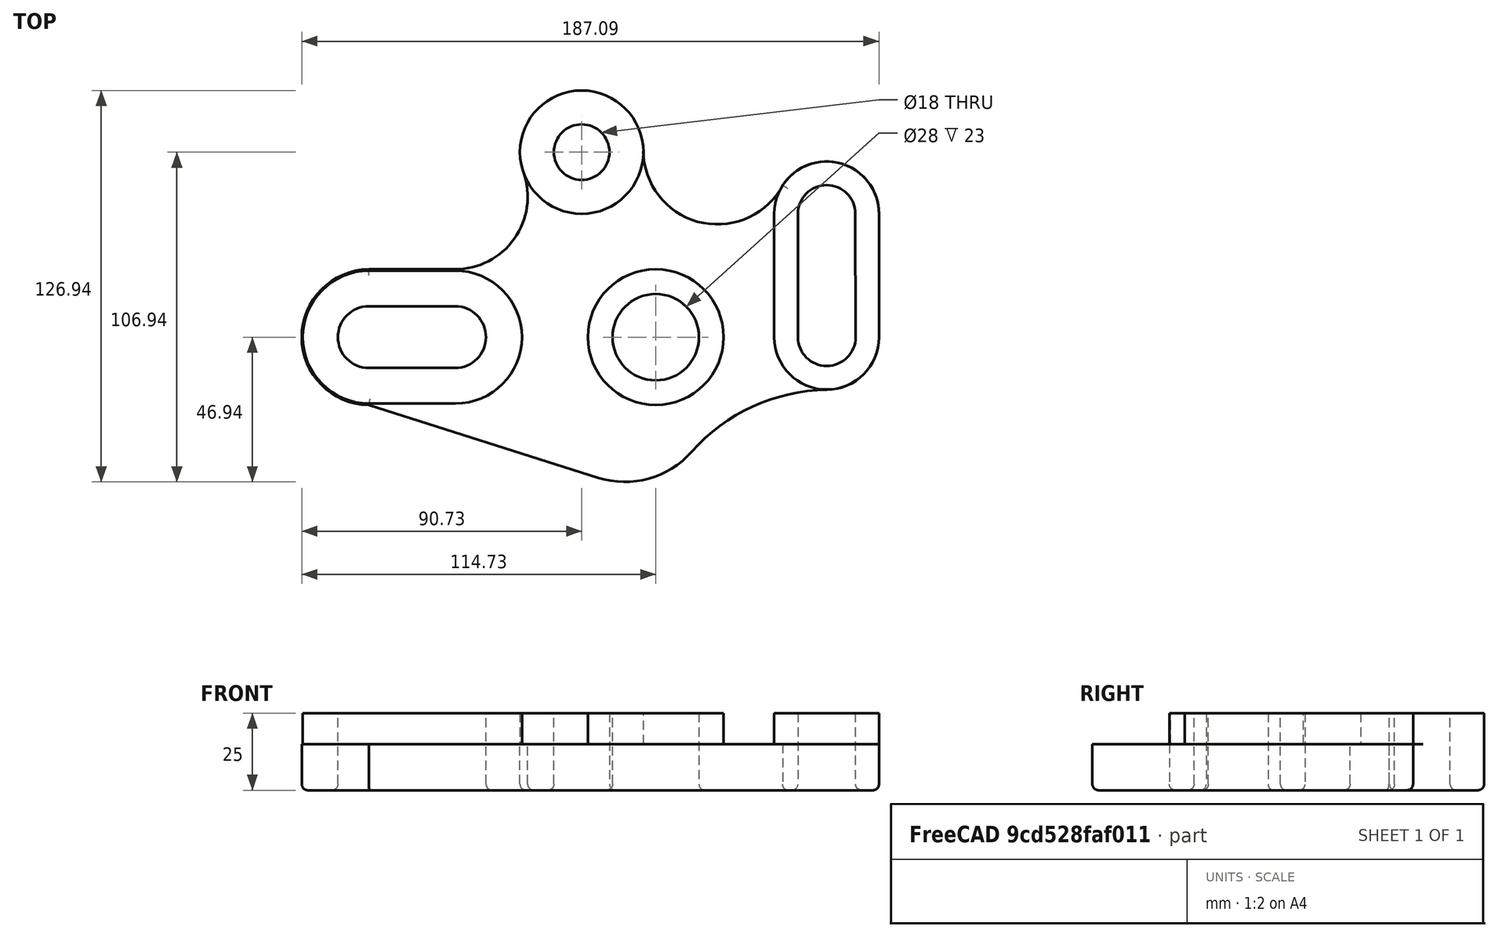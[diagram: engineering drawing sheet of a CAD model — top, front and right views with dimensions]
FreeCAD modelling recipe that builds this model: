
FCSTD DOCUMENT  (FreeCAD 0.19R24267 +148 (Git))
Label: Idler Plate
License: All rights reserved
LicenseURL: http://en.wikipedia.org/wiki/All_rights_reserved
objects: TechDraw::DrawViewDimension×26, Sketcher::SketchObject×4, PartDesign::Pad×2, PartDesign::Plane×1, Part::Part2DObjectPython×1, PartDesign::Pocket×1, PartDesign::Fillet×1, PartDesign::Body×1, TechDraw::DrawSVGTemplate×1, TechDraw::DrawViewPart×1, TechDraw::DrawPage×1
note: 15 computed .brp shape members not serialized (recipe doc carries the construction recipe); baked Part::Feature solids carry a one-line shape summary decoded from their .brp

FEATURE [Sketcher::SketchObject] Sketch
  FullyConstrained = false
  MapMode = 5
  Support = -> [XY_Plane]
  sketch-geometry (25):
    g0: Circle CenterX=-24 CenterY=60 CenterZ=0 NormalX=0 NormalY=0 NormalZ=1 AngleXU=0 Radius=20
    g1: Circle CenterX=0 CenterY=0 CenterZ=0 NormalX=0 NormalY=0 NormalZ=1 AngleXU=0 Radius=22
    g2: Circle CenterX=0 CenterY=0 CenterZ=0 NormalX=0 NormalY=0 NormalZ=1 AngleXU=0 Radius=14
    g3: Circle CenterX=-24 CenterY=60 CenterZ=0 NormalX=0 NormalY=0 NormalZ=1 AngleXU=0 Radius=9
    g4: ArcOfCircle CenterX=-93 CenterY=0 CenterZ=0 NormalX=0 NormalY=0 NormalZ=1 AngleXU=0 Radius=22 StartAngle=1.5708 EndAngle=4.71239
    g5: ArcOfCircle CenterX=-65 CenterY=-1.6e-15 CenterZ=0 NormalX=0 NormalY=0 NormalZ=1 AngleXU=0 Radius=22 StartAngle=4.71239 EndAngle=7.85398
    g6: LineSegment StartX=-93 StartY=-22 StartZ=0 EndX=-65 EndY=-22 EndZ=0
    g7: LineSegment StartX=-93 StartY=22 StartZ=0 EndX=-65 EndY=22 EndZ=0
    g8: ArcOfCircle CenterX=-93 CenterY=0 CenterZ=0 NormalX=0 NormalY=0 NormalZ=1 AngleXU=0 Radius=10 StartAngle=1.5708 EndAngle=4.71239
    g9: ArcOfCircle CenterX=-65 CenterY=-1.6e-15 CenterZ=0 NormalX=0 NormalY=0 NormalZ=1 AngleXU=0 Radius=10 StartAngle=4.71239 EndAngle=7.85398
    g10: LineSegment StartX=-93 StartY=-10 StartZ=0 EndX=-65 EndY=-10 EndZ=0
    g11: LineSegment StartX=-93 StartY=10 StartZ=0 EndX=-65 EndY=10 EndZ=0
    g12: ArcOfCircle CenterX=55.3868 CenterY=0 CenterZ=0 NormalX=0 NormalY=0 NormalZ=1 AngleXU=0 Radius=16.975 StartAngle=3.14159 EndAngle=6.28319
    g13: ArcOfCircle CenterX=55.3868 CenterY=40 CenterZ=0 NormalX=0 NormalY=0 NormalZ=1 AngleXU=0 Radius=16.975 StartAngle=0 EndAngle=3.14159
    g14: LineSegment StartX=72.3617 StartY=-4.2e-15 StartZ=0 EndX=72.3617 EndY=40 EndZ=0
    g15: LineSegment StartX=38.4118 StartY=2.1e-15 StartZ=0 EndX=38.4118 EndY=40 EndZ=0
    g16: ArcOfCircle CenterX=55.3868 CenterY=0 CenterZ=0 NormalX=0 NormalY=0 NormalZ=1 AngleXU=0 Radius=9.30464 StartAngle=3.14159 EndAngle=6.28319
    g17: ArcOfCircle CenterX=55.3868 CenterY=40 CenterZ=0 NormalX=0 NormalY=0 NormalZ=1 AngleXU=0 Radius=9.30464 StartAngle=2e-16 EndAngle=3.14159
    g18: LineSegment StartX=64.6914 StartY=-2.3e-15 StartZ=0 EndX=64.6914 EndY=40 EndZ=0
    g19: LineSegment StartX=46.0821 StartY=5.3e-15 StartZ=0 EndX=46.0821 EndY=40 EndZ=0
    g20: ArcOfCircle CenterX=-65 CenterY=45.4914 CenterZ=0 NormalX=0 NormalY=0 NormalZ=1 AngleXU=0 Radius=23.4914 StartAngle=4.71239 EndAngle=6.6233
    g21: ArcOfCircle CenterX=19.9961 CenterY=60.5875 CenterZ=0 NormalX=0 NormalY=0 NormalZ=1 AngleXU=0 Radius=24 StartAngle=3.15495 EndAngle=5.78943
    g22: LineSegment StartX=-93 StartY=-22 StartZ=0 EndX=-18.6679 EndY=-45.5803 EndZ=0
    g23: ArcOfCircle CenterX=56.0281 CenterY=-76.4776 CenterZ=0 NormalX=0 NormalY=0 NormalZ=1 AngleXU=0 Radius=59.5054 StartAngle=1.57918 EndAngle=2.41234
    g24: ArcOfCircle CenterX=-10.0673 CenterY=-18.4687 CenterZ=0 NormalX=0 NormalY=0 NormalZ=1 AngleXU=0 Radius=28.4431 StartAngle=4.4052 EndAngle=5.58151
  constraints (55):
    c: Coincident(g1,g-1)
    c: Coincident(g2,g1)
    c: Diameter(g1) = 44
    c: Diameter(g2) = 28
    c: Diameter(g0) = 40
    c: Coincident(g3,g0)
    c: Diameter(g3) = 18
    c: DistanceX(g0,g1) = 24
    c: DistanceY(g1,g0) = 60
    c: Tangent(g4,g7) = 1.5708
    c: Tangent(g4,g6) = -1.5708
    c: Tangent(g6,g5) = -1.5708
    c: Tangent(g7,g5) = 1.5708
    c: Horizontal(g6)
    c: Equal(g4,g5)
    c: PointOnObject(g4,g-1)
    c: Tangent(g8,g11) = 1.5708
    c: Tangent(g8,g10) = -1.5708
    c: Tangent(g10,g9) = -1.5708
    c: Tangent(g11,g9) = 1.5708
    c: Horizontal(g10)
    c: Coincident(g8,g4)
    c: Coincident(g5,g9)
    c: Radius(g4) = 22
    c: Radius(g8) = 10
    c: DistanceX(g4,g5) = 28
    c: Tangent(g12,g15) = 1.5708
    c: Tangent(g12,g14) = -1.5708
    c: Tangent(g14,g13) = -1.5708
    c: Tangent(g15,g13) = 1.5708
    c: Vertical(g14)
    c: Equal(g12,g13)
    c: PointOnObject(g12,g-1)
    c: Tangent(g16,g19) = 1.5708
    c: Tangent(g16,g18) = -1.5708
    c: Tangent(g18,g17) = -1.5708
    c: Tangent(g19,g17) = 1.5708
    c: Vertical(g18)
    c: Coincident(g16,g12)
    c: Coincident(g13,g17)
    c: DistanceY(g12,g13) = 40
    c: Coincident(g20,g5)
    c: PointOnObject(g20,g0)
    c: PointOnObject(g21,g13)
    c: PointOnObject(g21,g0)
    c: Tangent(g0,g21)
    c: Radius(g21) = 24
    c: Coincident(g22,g4)
    c: PointOnObject(g23,g12)
    c: Tangent(g23,g12)
    c: Coincident(g24,g23)
    c: Tangent(g24,g22) = -1.5708
    c: DistanceX(g5,g1) = 65
    c: Tangent(g0,g20)
    c: Tangent(g20,g7)
FEATURE [Sketcher::SketchObject] Sketch001
  ExternalGeometry = -> [Sketch]
  FullyConstrained = false
  MapMode = 5
  Support = -> [XY_Plane]
  sketch-geometry (11):
    g0: ArcOfCircle CenterX=-24 CenterY=60 CenterZ=0 NormalX=0 NormalY=0 NormalZ=1 AngleXU=0 Radius=20 StartAngle=0.0133524 EndAngle=3.48171
    g1: ArcOfCircle CenterX=19.9961 CenterY=60.5875 CenterZ=0 NormalX=0 NormalY=0 NormalZ=1 AngleXU=0 Radius=24 StartAngle=3.15495 EndAngle=5.78943
    g2: ArcOfCircle CenterX=55.3868 CenterY=40 CenterZ=0 NormalX=0 NormalY=0 NormalZ=1 AngleXU=0 Radius=16.975 StartAngle=-9e-16 EndAngle=2.5679
    g3: ArcOfCircle CenterX=55.248 CenterY=9.24041e-07 CenterZ=0 NormalX=0 NormalY=0 NormalZ=1 AngleXU=0 Radius=17.1138 StartAngle=4.7237 EndAngle=6.28319
    g4: ArcOfCircle CenterX=56.1121 CenterY=-76.3799 CenterZ=0 NormalX=0 NormalY=0 NormalZ=1 AngleXU=0 Radius=59.2711 StartAngle=1.58211 EndAngle=2.41888
    g5: ArcOfCircle CenterX=-9.97263 CenterY=-18.1014 CenterZ=0 NormalX=0 NormalY=0 NormalZ=1 AngleXU=0 Radius=28.8401 StartAngle=4.40589 EndAngle=5.56047
    g6: LineSegment StartX=-93 StartY=-22 StartZ=0 EndX=-18.6743 EndY=-45.5974 EndZ=0
    g7: ArcOfCircle CenterX=-92.7237 CenterY=2.42114e-05 CenterZ=0 NormalX=0 NormalY=0 NormalZ=1 AngleXU=0 Radius=22.0018 StartAngle=1.58353 EndAngle=4.69983
    g8: LineSegment StartX=72.3617 StartY=40 StartZ=0 EndX=72.3617 EndY=-5.68e-14 EndZ=0
    g9: LineSegment StartX=-93.0038 StartY=22 StartZ=0 EndX=-65 EndY=22 EndZ=0
    g10: ArcOfCircle CenterX=-65 CenterY=45.4914 CenterZ=0 NormalX=0 NormalY=0 NormalZ=1 AngleXU=0 Radius=23.4914 StartAngle=4.71239 EndAngle=6.6233
  constraints (24):
    c: Coincident(g0,g-13)
    c: Coincident(g0,g-4)
    c: Tangent(g0,g-3)
    c: Coincident(g1,g0)
    c: Coincident(g1,g-4)
    c: Tangent(g1,g-4)
    c: Coincident(g2,g1)
    c: Coincident(g2,g-6)
    c: Tangent(g2,g-5)
    c: Coincident(g3,g-7)
    c: Tangent(g3,g-7)
    c: Coincident(g7,g6)
    c: Coincident(g5,g6)
    c: Coincident(g8,g2)
    c: Coincident(g8,g3)
    c: Tangent(g4,g5) = 1.5708
    c: Tangent(g4,g3) = 1.5708
    c: Coincident(g6,g-11)
    c: Coincident(g9,g7)
    c: Coincident(g9,g-13)
    c: Horizontal(g9)
    c: Coincident(g10,g9)
    c: Coincident(g10,g0)
    c: Tangent(g10,g-13)
FEATURE [PartDesign::Pad] Pad
  Direction = (1,1,1)
  Length = 15
  Length2 = 100
  Profile = -> Sketch001
  Reversed = true
  Type = 0
FEATURE [Sketcher::SketchObject] Sketch002
  ExternalGeometry = -> [Sketch]
  FullyConstrained = false
  MapMode = 5
  Support = -> [XY_Plane]
  sketch-geometry (10):
    g0: Circle CenterX=0 CenterY=0 CenterZ=0 NormalX=0 NormalY=0 NormalZ=1 AngleXU=0 Radius=22
    g1: ArcOfCircle CenterX=55.3834 CenterY=-0.000158297 CenterZ=0 NormalX=0 NormalY=0 NormalZ=1 AngleXU=0 Radius=16.9716 StartAngle=3.14159 EndAngle=6.28319
    g2: ArcOfCircle CenterX=55.3834 CenterY=39.9998 CenterZ=0 NormalX=0 NormalY=0 NormalZ=1 AngleXU=0 Radius=16.9716 StartAngle=2.61945e-11 EndAngle=3.14159
    g3: LineSegment StartX=72.3549 StartY=-0.000158298 StartZ=0 EndX=72.3549 EndY=39.9998 EndZ=0
    g4: LineSegment StartX=38.4118 StartY=-0.000158298 StartZ=0 EndX=38.4118 EndY=39.9998 EndZ=0
    g5: ArcOfCircle CenterX=-64.8801 CenterY=0 CenterZ=0 NormalX=0 NormalY=0 NormalZ=1 AngleXU=0 Radius=21.5308 StartAngle=4.71239 EndAngle=7.85398
    g6: ArcOfCircle CenterX=-92.8801 CenterY=-1.3e-15 CenterZ=0 NormalX=0 NormalY=0 NormalZ=1 AngleXU=0 Radius=21.5308 StartAngle=1.5708 EndAngle=4.71239
    g7: LineSegment StartX=-64.8801 StartY=21.5308 StartZ=0 EndX=-92.8801 EndY=21.5308 EndZ=0
    g8: LineSegment StartX=-64.8801 StartY=-21.5308 StartZ=0 EndX=-92.8801 EndY=-21.5308 EndZ=0
    g9: Circle CenterX=-24 CenterY=60 CenterZ=0 NormalX=0 NormalY=0 NormalZ=1 AngleXU=0 Radius=20
  constraints (20):
    c: Coincident(g0,g-1)
    c: Tangent(g1,g4) = 1.5708
    c: Tangent(g1,g3) = -1.5708
    c: Tangent(g3,g2) = -1.5708
    c: Tangent(g4,g2) = 1.5708
    c: Vertical(g3)
    c: Equal(g1,g2)
    c: PointOnObject(g2,g-7)
    c: Tangent(g5,g8) = 1.5708
    c: Tangent(g5,g7) = -1.5708
    c: Tangent(g7,g6) = -1.5708
    c: Tangent(g8,g6) = 1.5708
    c: Horizontal(g7)
    c: Equal(g5,g6)
    c: PointOnObject(g5,g-1)
    c: DistanceX(g6,g5) = 28
    c: DistanceY(g1,g2) = 40
    c: Coincident(g9,g-8)
    c: Diameter(g9) = 40
    c: Diameter(g0) = 44
FEATURE [PartDesign::Pad] Pad001
  BaseFeature = -> Pad
  Direction = (1,1,1)
  Length = 10
  Length2 = 100
  Profile = -> Sketch002
  Type = 0
FEATURE [PartDesign::Plane] DatumPlane
  Length = 217.722
  MapMode = 5
  Placement = pos=(0,0,10) rot=(0,0,1;0rad)
  ResizeMode = 0
  Support = -> [Pad001]
  Width = 157.601
FEATURE [Sketcher::SketchObject] Sketch003
  ExternalGeometry = -> [Sketch]
  FullyConstrained = false
  MapMode = 5
  Placement = pos=(0,0,10) rot=(0,0,1;0rad)
  Support = -> [DatumPlane]
  sketch-geometry (10):
    g0: Circle CenterX=0 CenterY=0 CenterZ=0 NormalX=0 NormalY=0 NormalZ=1 AngleXU=0 Radius=14
    g1: Circle CenterX=-24 CenterY=60 CenterZ=0 NormalX=0 NormalY=0 NormalZ=1 AngleXU=0 Radius=9
    g2: ArcOfCircle CenterX=-65 CenterY=0 CenterZ=0 NormalX=0 NormalY=0 NormalZ=1 AngleXU=0 Radius=10 StartAngle=4.71239 EndAngle=7.85398
    g3: ArcOfCircle CenterX=-93 CenterY=4.585e-13 CenterZ=0 NormalX=0 NormalY=0 NormalZ=1 AngleXU=0 Radius=10 StartAngle=1.5708 EndAngle=4.71239
    g4: LineSegment StartX=-65 StartY=10 StartZ=0 EndX=-93 EndY=10 EndZ=0
    g5: LineSegment StartX=-65 StartY=-10 StartZ=0 EndX=-93 EndY=-10 EndZ=0
    g6: ArcOfCircle CenterX=55.4299 CenterY=1.4e-15 CenterZ=0 NormalX=0 NormalY=0 NormalZ=1 AngleXU=0 Radius=9.34777 StartAngle=3.14159 EndAngle=6.27883
    g7: ArcOfCircle CenterX=55.3868 CenterY=40 CenterZ=0 NormalX=0 NormalY=0 NormalZ=1 AngleXU=0 Radius=9.30464 StartAngle=0 EndAngle=3.14159
    g8: LineSegment StartX=64.7776 StartY=-0.04075 StartZ=0 EndX=64.6914 EndY=40 EndZ=0
    g9: LineSegment StartX=46.0821 StartY=5.3e-15 StartZ=0 EndX=46.0821 EndY=40 EndZ=0
  constraints (21):
    c: Coincident(g0,g-1)
    c: Diameter(g0) = 28
    c: Coincident(g1,g-3)
    c: Diameter(g1) = 18
    c: Tangent(g2,g5) = 1.5708
    c: Tangent(g2,g4) = -1.5708
    c: Tangent(g4,g3) = -1.5708
    c: Tangent(g5,g3) = 1.5708
    c: Horizontal(g4)
    c: Equal(g2,g3)
    c: PointOnObject(g2,g-1)
    c: Distance(g2,g3) = 28
    c: Diameter(g3) = 20
    c: DistanceX(g2,g0) = 65
    c: Tangent(g6,g9) = 1.5708
    c: Tangent(g9,g7) = 1.5708
    c: Coincident(g7,g-5)
    c: Coincident(g6,g-7)
    c: Coincident(g7,g8)
    c: Coincident(g7,g-6)
    c: Coincident(g8,g6)
FEATURE [Part::Part2DObjectPython] Clone2D  label="Sketch (2D)"  # Draft 2D object (typed FeaturePython)
  Fuse = false
  Objects = -> [Sketch]
  Scale = (1,1,1)
FEATURE [PartDesign::Pocket] Pocket
  BaseFeature = -> Pad001
  Length = 3
  Length2 = 100
  Profile = -> Sketch003
  Type = 1
FEATURE [PartDesign::Fillet] Fillet
  Base = -> Pocket [Edge33,Edge35,Edge37,Edge41,Edge42,Edge39,Edge40,Edge38,Edge36,Edge48,Edge43,Edge34,Edge32,Edge10,Edge4,Edge7,Edge31,Edge47,Edge46,Edge45,Edge44]
  BaseFeature = -> Pocket
  Radius = 2
  SupportTransform = false
FEATURE [PartDesign::Body] Body
  Group = -> [Sketch,Sketch001,Pad,Sketch002,Pad001,DatumPlane,Sketch003,Clone2D,Pocket,Fillet]
  Origin = -> Origin
  Tip = -> Fillet
FEATURE [TechDraw::DrawSVGTemplate] Template
  EditableTexts = Designed_by_Name=Designed by Name; Drawing_number=Drawing number; FC-Date=Date; FC-SC=Scale; FC-SH=Sheet; FC-Title=Title; Subtitle=Subtitle; Weight=Weight
  Height = 210
  Orientation = 1
  Width = 297
FEATURE [TechDraw::DrawViewPart] View  label="Top view"
  CoarseView = false
  Direction = (0,0,1)
  Focus = 100
  HardHidden = false
  IsoCount = 0
  IsoHidden = false
  IsoVisible = false
  LockPosition = false
  Perspective = false
  Rotation = 0
  ScaleType = 0
  SeamHidden = false
  SeamVisible = true
  SmoothHidden = false
  SmoothVisible = true
  Source = -> [Fillet]
  X = 110.865
  XDirection = (-1,0,0)
  Y = 128.572
FEATURE [TechDraw::DrawViewDimension] Dimension
  Arbitrary = false
  ArbitraryTolerances = false
  EqualTolerance = true
  FormatSpec = ⌀%.2f
  FormatSpecOverTolerance = %+.2f
  FormatSpecUnderTolerance = %+.2f
  Inverted = false
  LockPosition = false
  MeasureType = 1
  OverTolerance = 0
  References2D = -> [View]
  Rotation = 0
  ScaleType = 0
  TheoreticalExact = false
  Type = 5
  UnderTolerance = 0
  X = -39.4982
  Y = 38.3834
FEATURE [TechDraw::DrawViewDimension] Dimension001
  Arbitrary = false
  ArbitraryTolerances = false
  EqualTolerance = true
  FormatSpec = ⌀%.2f
  FormatSpecOverTolerance = %+.2f
  FormatSpecUnderTolerance = %+.2f
  Inverted = false
  LockPosition = false
  MeasureType = 1
  OverTolerance = 0
  References2D = -> [View]
  Rotation = 0
  ScaleType = 0
  TheoreticalExact = false
  Type = 5
  UnderTolerance = 0
  X = 7.12678
  Y = 44.872
FEATURE [TechDraw::DrawViewDimension] Dimension002
  Arbitrary = false
  ArbitraryTolerances = false
  EqualTolerance = true
  FormatSpec = %.2f
  FormatSpecOverTolerance = %+.2f
  FormatSpecUnderTolerance = %+.2f
  Inverted = false
  LockPosition = false
  MeasureType = 1
  OverTolerance = 0
  References2D = -> [View]
  Rotation = 0
  ScaleType = 0
  TheoreticalExact = false
  Type = 6
  UnderTolerance = 0
  X = 18.4646
  Y = 51.2195
FEATURE [TechDraw::DrawViewDimension] Dimension003
  Arbitrary = false
  ArbitraryTolerances = false
  EqualTolerance = true
  FormatSpec = R%.2f
  FormatSpecOverTolerance = %+.2f
  FormatSpecUnderTolerance = %+.2f
  Inverted = false
  LockPosition = false
  MeasureType = 1
  OverTolerance = 0
  References2D = -> [View]
  Rotation = 0
  ScaleType = 0
  TheoreticalExact = false
  Type = 4
  UnderTolerance = 0
  X = -80.4146
  Y = 59.9268
FEATURE [TechDraw::DrawViewDimension] Dimension004
  Arbitrary = false
  ArbitraryTolerances = false
  EqualTolerance = true
  FormatSpec = R%.2f
  FormatSpecOverTolerance = %+.2f
  FormatSpecUnderTolerance = %+.2f
  Inverted = false
  LockPosition = false
  MeasureType = 1
  OverTolerance = 0
  References2D = -> [View]
  Rotation = 0
  ScaleType = 0
  TheoreticalExact = false
  Type = 4
  UnderTolerance = 0
  X = -26.3197
  Y = 57.6329
FEATURE [TechDraw::DrawViewDimension] Dimension005
  Arbitrary = false
  ArbitraryTolerances = false
  EqualTolerance = true
  FormatSpec = ⌀%.2f
  FormatSpecOverTolerance = %+.2f
  FormatSpecUnderTolerance = %+.2f
  Inverted = false
  LockPosition = false
  MeasureType = 1
  OverTolerance = 0
  References2D = -> [View]
  Rotation = 0
  ScaleType = 0
  TheoreticalExact = false
  Type = 5
  UnderTolerance = 0
  X = 3.22632
  Y = -6.83704
FEATURE [TechDraw::DrawViewDimension] Dimension006
  Arbitrary = false
  ArbitraryTolerances = false
  EqualTolerance = true
  FormatSpec = ⌀%.2f
  FormatSpecOverTolerance = %+.2f
  FormatSpecUnderTolerance = %+.2f
  Inverted = false
  LockPosition = false
  MeasureType = 1
  OverTolerance = 0
  References2D = -> [View]
  Rotation = 0
  ScaleType = 0
  TheoreticalExact = false
  Type = 5
  UnderTolerance = 0
  X = 12.8049
  Y = -4.60976
FEATURE [TechDraw::DrawViewDimension] Dimension007
  Arbitrary = false
  ArbitraryTolerances = false
  EqualTolerance = true
  FormatSpec = R%.2f
  FormatSpecOverTolerance = %+.2f
  FormatSpecUnderTolerance = %+.2f
  Inverted = false
  LockPosition = false
  MeasureType = 1
  OverTolerance = 0
  References2D = -> [View]
  Rotation = 0
  ScaleType = 0
  TheoreticalExact = false
  Type = 4
  UnderTolerance = 0
  X = -54.8941
  Y = 33.9773
FEATURE [TechDraw::DrawViewDimension] Dimension008
  Arbitrary = false
  ArbitraryTolerances = false
  EqualTolerance = true
  FormatSpec = R%.2f
  FormatSpecOverTolerance = %+.2f
  FormatSpecUnderTolerance = %+.2f
  Inverted = false
  LockPosition = false
  MeasureType = 1
  OverTolerance = 0
  References2D = -> [View]
  Rotation = 0
  ScaleType = 0
  TheoreticalExact = false
  Type = 4
  UnderTolerance = 0
  X = -83.1947
  Y = 40.3427
FEATURE [TechDraw::DrawViewDimension] Dimension009
  Arbitrary = false
  ArbitraryTolerances = false
  EqualTolerance = true
  FormatSpec = R%.2f
  FormatSpecOverTolerance = %+.2f
  FormatSpecUnderTolerance = %+.2f
  Inverted = false
  LockPosition = false
  MeasureType = 1
  OverTolerance = 0
  References2D = -> [View]
  Rotation = 0
  ScaleType = 0
  TheoreticalExact = false
  Type = 4
  UnderTolerance = 0
  X = 52.7561
  Y = -32.7805
FEATURE [TechDraw::DrawViewDimension] Dimension010
  Arbitrary = false
  ArbitraryTolerances = false
  EqualTolerance = true
  FormatSpec = R%.2f
  FormatSpecOverTolerance = %+.2f
  FormatSpecUnderTolerance = %+.2f
  Inverted = false
  LockPosition = false
  MeasureType = 1
  OverTolerance = 0
  References2D = -> [View]
  Rotation = 0
  ScaleType = 0
  TheoreticalExact = false
  Type = 4
  UnderTolerance = 0
  X = -42.8604
  Y = -5.8446
FEATURE [TechDraw::DrawViewDimension] Dimension012
  Arbitrary = false
  ArbitraryTolerances = false
  EqualTolerance = true
  FormatSpec = %.2f
  FormatSpecOverTolerance = %+.2f
  FormatSpecUnderTolerance = %+.2f
  Inverted = false
  LockPosition = false
  MeasureType = 1
  OverTolerance = 0
  References2D = -> [View]
  Rotation = 0
  ScaleType = 0
  TheoreticalExact = false
  Type = 1
  UnderTolerance = 0
  X = -90.2951
  Y = -50.3832
FEATURE [TechDraw::DrawViewDimension] Dimension013
  Arbitrary = false
  ArbitraryTolerances = false
  EqualTolerance = true
  FormatSpec = %.2f
  FormatSpecOverTolerance = %+.2f
  FormatSpecUnderTolerance = %+.2f
  Inverted = false
  LockPosition = false
  MeasureType = 1
  OverTolerance = 0
  References2D = -> [View]
  Rotation = 0
  ScaleType = 0
  TheoreticalExact = false
  Type = 2
  UnderTolerance = 0
  X = 63.765
  Y = -14.4595
FEATURE [TechDraw::DrawViewDimension] Dimension014
  Arbitrary = false
  ArbitraryTolerances = false
  EqualTolerance = true
  FormatSpec = %.2f
  FormatSpecOverTolerance = %+.2f
  FormatSpecUnderTolerance = %+.2f
  Inverted = false
  LockPosition = false
  MeasureType = 1
  OverTolerance = 0
  References2D = -> [View]
  Rotation = 0
  ScaleType = 0
  TheoreticalExact = false
  Type = 1
  UnderTolerance = 0
  X = 36.7328
  Y = 64.093
FEATURE [TechDraw::DrawViewDimension] Dimension015
  Arbitrary = false
  ArbitraryTolerances = false
  EqualTolerance = true
  FormatSpec = R%.2f
  FormatSpecOverTolerance = %+.2f
  FormatSpecUnderTolerance = %+.2f
  Inverted = false
  LockPosition = false
  MeasureType = 1
  OverTolerance = 0
  References2D = -> [View]
  Rotation = 0
  ScaleType = 0
  TheoreticalExact = false
  Type = 4
  UnderTolerance = 0
  X = 50.0298
  Y = 23.3784
FEATURE [TechDraw::DrawViewDimension] Dimension016
  Arbitrary = false
  ArbitraryTolerances = false
  EqualTolerance = true
  FormatSpec = R%.2f
  FormatSpecOverTolerance = %+.2f
  FormatSpecUnderTolerance = %+.2f
  Inverted = false
  LockPosition = false
  MeasureType = 1
  OverTolerance = 0
  References2D = -> [View]
  Rotation = 0
  ScaleType = 0
  TheoreticalExact = false
  Type = 4
  UnderTolerance = 0
  X = 46.2892
  Y = 32.7298
FEATURE [TechDraw::DrawViewDimension] Dimension017
  Arbitrary = false
  ArbitraryTolerances = false
  EqualTolerance = true
  FormatSpec = %.2f
  FormatSpecOverTolerance = %+.2f
  FormatSpecUnderTolerance = %+.2f
  Inverted = false
  LockPosition = false
  MeasureType = 1
  OverTolerance = 0
  References2D = -> [View]
  Rotation = 0
  ScaleType = 0
  TheoreticalExact = false
  Type = 1
  UnderTolerance = 0
  X = 57.4978
  Y = -5.57445
FEATURE [TechDraw::DrawViewDimension] Dimension018
  Arbitrary = false
  ArbitraryTolerances = false
  EqualTolerance = true
  FormatSpec = %.2f
  FormatSpecOverTolerance = %+.2f
  FormatSpecUnderTolerance = %+.2f
  Inverted = false
  LockPosition = false
  MeasureType = 1
  OverTolerance = 0
  References2D = -> [View]
  Rotation = 0
  ScaleType = 0
  TheoreticalExact = false
  Type = 1
  UnderTolerance = 0
  X = -62.6941
  Y = -60.5139
FEATURE [TechDraw::DrawViewDimension] Dimension019
  Arbitrary = false
  ArbitraryTolerances = false
  EqualTolerance = true
  FormatSpec = %.2f
  FormatSpecOverTolerance = %+.2f
  FormatSpecUnderTolerance = %+.2f
  Inverted = false
  LockPosition = false
  MeasureType = 1
  OverTolerance = 0
  References2D = -> [View]
  Rotation = 0
  ScaleType = 0
  TheoreticalExact = false
  Type = 2
  UnderTolerance = 0
  X = 97.274
  Y = -3.08202
FEATURE [TechDraw::DrawViewDimension] Dimension020
  Arbitrary = false
  ArbitraryTolerances = false
  EqualTolerance = true
  FormatSpec = %.2f
  FormatSpecOverTolerance = %+.2f
  FormatSpecUnderTolerance = %+.2f
  Inverted = false
  LockPosition = false
  MeasureType = 1
  OverTolerance = 0
  References2D = -> [View]
  Rotation = 0
  ScaleType = 0
  TheoreticalExact = false
  Type = 2
  UnderTolerance = 0
  X = 98.2091
  Y = 32.1894
FEATURE [TechDraw::DrawViewDimension] Dimension021
  Arbitrary = false
  ArbitraryTolerances = false
  EqualTolerance = true
  FormatSpec = %.2f
  FormatSpecOverTolerance = %+.2f
  FormatSpecUnderTolerance = %+.2f
  Inverted = false
  LockPosition = false
  MeasureType = 1
  OverTolerance = 0
  References2D = -> [View]
  Rotation = 0
  ScaleType = 0
  TheoreticalExact = false
  Type = 0
  UnderTolerance = 0
  X = 67.085
  Y = -55.138
FEATURE [TechDraw::DrawViewDimension] Dimension022
  Arbitrary = false
  ArbitraryTolerances = false
  EqualTolerance = true
  FormatSpec = %.2f
  FormatSpecOverTolerance = %+.2f
  FormatSpecUnderTolerance = %+.2f
  Inverted = false
  LockPosition = false
  MeasureType = 1
  OverTolerance = 0
  References2D = -> [View]
  Rotation = 0
  ScaleType = 0
  TheoreticalExact = false
  Type = 0
  UnderTolerance = 0
  X = -43.22
  Y = -43.7934
FEATURE [TechDraw::DrawViewDimension] Dimension023
  Arbitrary = false
  ArbitraryTolerances = false
  EqualTolerance = true
  FormatSpec = %.2f
  FormatSpecOverTolerance = %+.2f
  FormatSpecUnderTolerance = %+.2f
  Inverted = false
  LockPosition = false
  MeasureType = 1
  OverTolerance = 0
  References2D = -> [View]
  Rotation = 0
  ScaleType = 0
  TheoreticalExact = false
  Type = 0
  UnderTolerance = 0
  X = -61.4779
  Y = 56.193
FEATURE [TechDraw::DrawViewDimension] Dimension024
  Arbitrary = false
  ArbitraryTolerances = false
  EqualTolerance = true
  FormatSpec = %.2f
  FormatSpecOverTolerance = %+.2f
  FormatSpecUnderTolerance = %+.2f
  Inverted = false
  LockPosition = false
  MeasureType = 1
  OverTolerance = 0
  References2D = -> [View]
  Rotation = 0
  ScaleType = 0
  TheoreticalExact = false
  Type = 0
  UnderTolerance = 0
  X = -10.8605
  Y = 50.33
FEATURE [TechDraw::DrawViewDimension] Dimension025
  Arbitrary = false
  ArbitraryTolerances = false
  EqualTolerance = true
  FormatSpec = %.2f
  FormatSpecOverTolerance = %+.2f
  FormatSpecUnderTolerance = %+.2f
  Inverted = false
  LockPosition = false
  MeasureType = 1
  OverTolerance = 0
  References2D = -> [View]
  Rotation = 0
  ScaleType = 0
  TheoreticalExact = false
  Type = 1
  UnderTolerance = 0
  X = -51.539
  Y = 11.2807
FEATURE [TechDraw::DrawViewDimension] Dimension026
  Arbitrary = false
  ArbitraryTolerances = false
  EqualTolerance = true
  FormatSpec = %.2f
  FormatSpecOverTolerance = %+.2f
  FormatSpecUnderTolerance = %+.2f
  Inverted = false
  LockPosition = false
  MeasureType = 1
  OverTolerance = 0
  References2D = -> [View]
  Rotation = 0
  ScaleType = 0
  TheoreticalExact = false
  Type = 1
  UnderTolerance = 0
  X = -19.8309
  Y = -17.3922
FEATURE [TechDraw::DrawPage] Page
  KeepUpdated = true
  NextBalloonIndex = 1
  ProjectionType = 0
  Template = -> Template
  Views = -> [View,Dimension,Dimension001,Dimension002,Dimension003,Dimension004,Dimension005,Dimension006,Dimension007,Dimension008,Dimension009,Dimension010,Dimension012,Dimension013,Dimension014,Dimension015,Dimension016,Dimension017,Dimension018,Dimension019,Dimension020,Dimension021,Dimension022,Dimension023,Dimension024,Dimension025,Dimension026]
